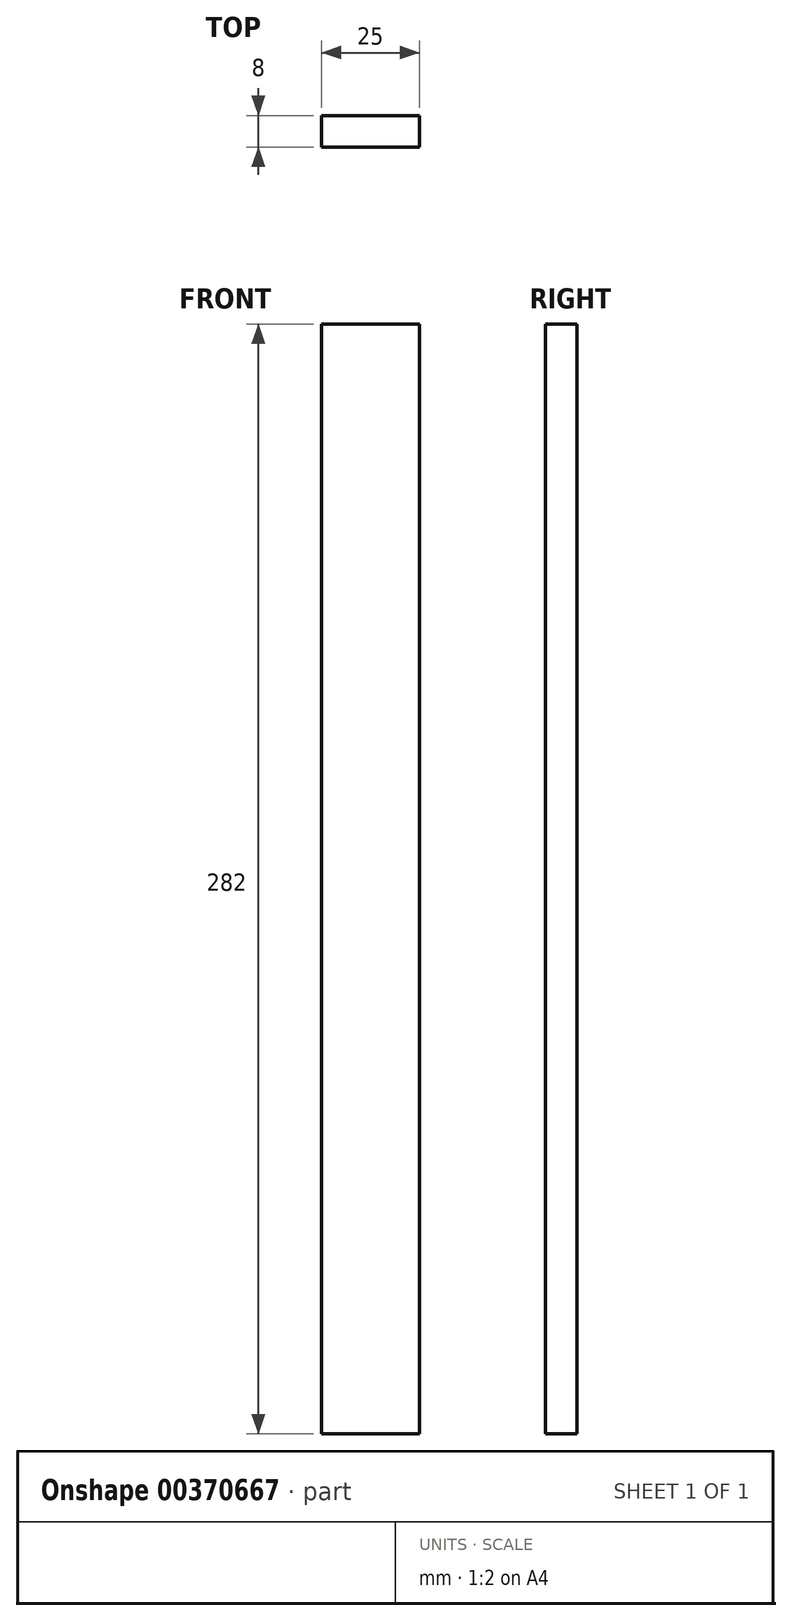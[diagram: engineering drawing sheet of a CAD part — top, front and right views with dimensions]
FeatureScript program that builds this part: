
annotation { "Feature Type Name" : "Feature", "Feature Type Description" : "" }
export const myFeature = defineFeature(function(context is Context, id is Id, definition is map)
    precondition{}
    {
        {
            var Q0;
            Q0=qCreatedBy(makeId("Front.planeOp"),FACE);
            var sketch = newSketch(context, id + "F0", { "sketchPlane" : qUnion([Q0])});
            skLineSegment(sketch, "E0.bottom", {"start": v(0, 0) * mm, "end": v(25, 0) * mm});
            skLineSegment(sketch, "E0.top", {"start": v(0, -282) * mm, "end": v(25, -282) * mm});
            skLineSegment(sketch, "E0.left", {"start": v(0, 0) * mm, "end": v(0, -282) * mm});
            skLineSegment(sketch, "E0.right", {"start": v(25, 0) * mm, "end": v(25, -282) * mm});
            skSolve(sketch);
        }
        {
            var Q0;
            Q0 = qSketchRegion(id + "F0", true);
            extrude(context, id + "F1", {"entities" : qUnion([Q0]), "depth" : 8 * mm});
        }
    });
